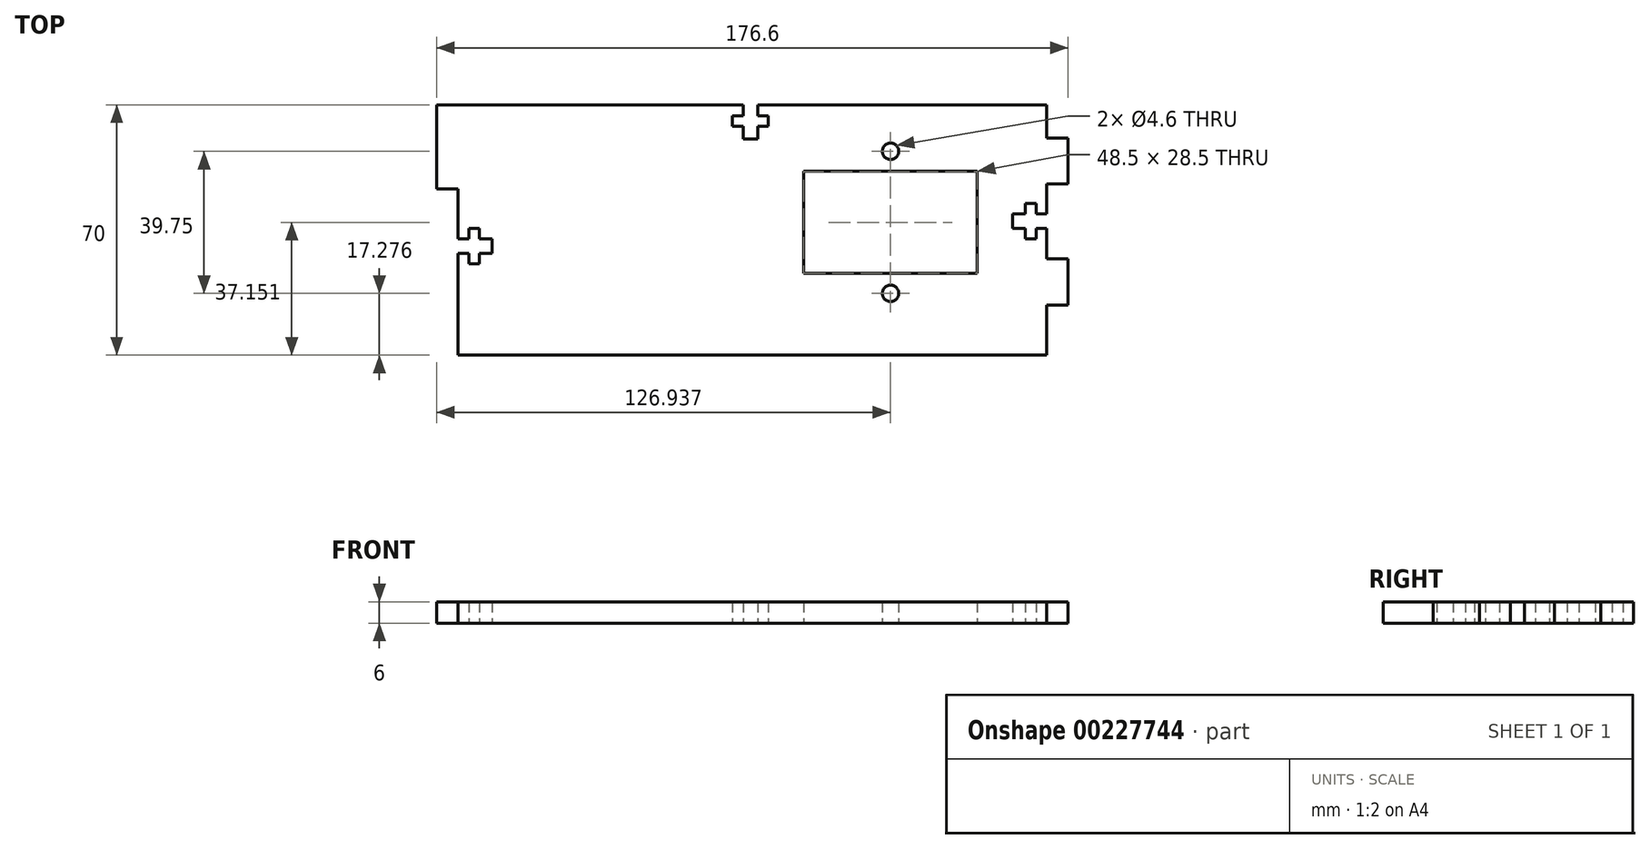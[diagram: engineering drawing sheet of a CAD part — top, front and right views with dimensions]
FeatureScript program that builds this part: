
annotation { "Feature Type Name" : "Feature", "Feature Type Description" : "" }
export const myFeature = defineFeature(function(context is Context, id is Id, definition is map)
    precondition{}
    {
        {
            var Q0;
            Q0=qCreatedBy(makeId("Top.planeOp"),FACE);
            var sketch = newSketch(context, id + "F0", { "sketchPlane" : qUnion([Q0])});
            skLineSegment(sketch, "E0.bottom", {"start": v(-82.3, 35) * mm, "end": v(82.3, 35) * mm});
            skLineSegment(sketch, "E0.top", {"start": v(-82.3, -35) * mm, "end": v(82.3, -35) * mm});
            skLineSegment(sketch, "E0.left", {"start": v(-82.3, 35) * mm, "end": v(-82.3, -35) * mm});
            skLineSegment(sketch, "E0.right", {"start": v(82.3, 35) * mm, "end": v(82.3, -35) * mm});
            skPoint(sketch, "E0.middle", {"position": v(0, 0) * mm});
            skLineSegment(sketch, "E1.bottom", {"start": v(82.3, 25.75) * mm, "end": v(88.3, 25.75) * mm});
            skLineSegment(sketch, "E1.top", {"start": v(82.3, 12.85) * mm, "end": v(88.3, 12.85) * mm});
            skLineSegment(sketch, "E1.left", {"start": v(82.3, 25.75) * mm, "end": v(82.3, 12.85) * mm});
            skLineSegment(sketch, "E1.right", {"start": v(88.3, 25.75) * mm, "end": v(88.3, 12.85) * mm});
            skLineSegment(sketch, "E2.bottom", {"start": v(82.3, -8.1) * mm, "end": v(88.3, -8.1) * mm});
            skLineSegment(sketch, "E2.top", {"start": v(82.3, -21) * mm, "end": v(88.3, -21) * mm});
            skLineSegment(sketch, "E2.left", {"start": v(82.3, -8.1) * mm, "end": v(82.3, -21) * mm});
            skLineSegment(sketch, "E2.right", {"start": v(88.3, -8.1) * mm, "end": v(88.3, -21) * mm});
            skLineSegment(sketch, "E3.bottom", {"start": v(-62.5, 35) * mm, "end": v(-23.3, 35) * mm});
            skLineSegment(sketch, "E3.top", {"start": v(-62.5, 41) * mm, "end": v(-23.3, 41) * mm});
            skLineSegment(sketch, "E3.left", {"start": v(-62.5, 35) * mm, "end": v(-62.5, 41) * mm});
            skLineSegment(sketch, "E3.right", {"start": v(-23.3, 35) * mm, "end": v(-23.3, 41) * mm});
            skLineSegment(sketch, "E4.bottom", {"start": v(22.1, 35) * mm, "end": v(61.3, 35) * mm});
            skLineSegment(sketch, "E4.top", {"start": v(22.1, 41) * mm, "end": v(61.3, 41) * mm});
            skLineSegment(sketch, "E4.left", {"start": v(22.1, 35) * mm, "end": v(22.1, 41) * mm});
            skLineSegment(sketch, "E4.right", {"start": v(61.3, 35) * mm, "end": v(61.3, 41) * mm});
            skLineSegment(sketch, "E5.bottom", {"start": v(-82.3, 35) * mm, "end": v(-88.3, 35) * mm});
            skLineSegment(sketch, "E5.top", {"start": v(-82.3, 11.5) * mm, "end": v(-88.3, 11.5) * mm});
            skLineSegment(sketch, "E5.left", {"start": v(-82.3, 35) * mm, "end": v(-82.3, 11.5) * mm});
            skLineSegment(sketch, "E5.right", {"start": v(-88.3, 35) * mm, "end": v(-88.3, 11.5) * mm});
            skLineSegment(sketch, "E6", {"start": v(-82.3, -2.5) * mm, "end": v(-79.3, -2.5) * mm});
            skLineSegment(sketch, "E7", {"start": v(-79.3, -2.5) * mm, "end": v(-79.3, 0.5) * mm});
            skLineSegment(sketch, "E8", {"start": v(-79.3, 0.5) * mm, "end": v(-76.3, 0.5) * mm});
            skLineSegment(sketch, "E9", {"start": v(-76.3, 0.5) * mm, "end": v(-76.3, -2.5) * mm});
            skLineSegment(sketch, "E10", {"start": v(-76.3, -2.5) * mm, "end": v(-72.8, -2.5) * mm});
            skLineSegment(sketch, "E11", {"start": v(-72.8, -2.5) * mm, "end": v(-72.8, -4.5) * mm});
            skLineSegment(sketch, "E12", {"start": v(-72.8, -4.5) * mm, "end": v(-82.3, -4.5) * mm, "construction": true});
            skLineSegment(sketch, "E13.MirrorCS", {"start": v(-82.3, -6.5) * mm, "end": v(-79.3, -6.5) * mm});
            skLineSegment(sketch, "E14.MirrorCS", {"start": v(-79.3, -6.5) * mm, "end": v(-79.3, -9.5) * mm});
            skLineSegment(sketch, "E15.MirrorCS", {"start": v(-76.3, -6.5) * mm, "end": v(-72.8, -6.5) * mm});
            skLineSegment(sketch, "E16.MirrorCS", {"start": v(-79.3, -9.5) * mm, "end": v(-76.3, -9.5) * mm});
            skLineSegment(sketch, "E17.MirrorCS", {"start": v(-72.8, -6.5) * mm, "end": v(-72.8, -4.5) * mm});
            skLineSegment(sketch, "E18.MirrorCS", {"start": v(-76.3, -9.5) * mm, "end": v(-76.3, -6.5) * mm});
            skLineSegment(sketch, "E19", {"start": v(72.8, 4.5) * mm, "end": v(76.3, 4.5) * mm});
            skLineSegment(sketch, "E20", {"start": v(76.3, 4.5) * mm, "end": v(76.3, 7.5) * mm});
            skLineSegment(sketch, "E21", {"start": v(76.3, 7.5) * mm, "end": v(79.3, 7.5) * mm});
            skLineSegment(sketch, "E22", {"start": v(79.3, 7.5) * mm, "end": v(79.3, 4.5) * mm});
            skLineSegment(sketch, "E23", {"start": v(79.3, 4.5) * mm, "end": v(82.3, 4.5) * mm});
            skLineSegment(sketch, "E24", {"start": v(82.3, 4.5) * mm, "end": v(82.3, 2.5) * mm});
            skLineSegment(sketch, "E25", {"start": v(82.3, 2.5) * mm, "end": v(72.8, 2.5) * mm, "construction": true});
            skLineSegment(sketch, "E26.MirrorCS", {"start": v(72.8, 0.5) * mm, "end": v(76.3, 0.5) * mm});
            skLineSegment(sketch, "E27.MirrorCS", {"start": v(76.3, 0.5) * mm, "end": v(76.3, -2.5) * mm});
            skLineSegment(sketch, "E28.MirrorCS", {"start": v(79.3, 0.5) * mm, "end": v(82.3, 0.5) * mm});
            skLineSegment(sketch, "E29.MirrorCS", {"start": v(76.3, -2.5) * mm, "end": v(79.3, -2.5) * mm});
            skLineSegment(sketch, "E30.MirrorCS", {"start": v(82.3, 0.5) * mm, "end": v(82.3, 2.5) * mm});
            skLineSegment(sketch, "E31.MirrorCS", {"start": v(79.3, -2.5) * mm, "end": v(79.3, 0.5) * mm});
            skLineSegment(sketch, "E32", {"start": v(72.8, 0.5) * mm, "end": v(72.8, 4.5) * mm});
            skLineSegment(sketch, "E33", {"start": v(-5.55, 32) * mm, "end": v(-2.55, 32) * mm});
            skLineSegment(sketch, "E34", {"start": v(-2.55, 32) * mm, "end": v(-2.55, 35) * mm});
            skLineSegment(sketch, "E35", {"start": v(-2.55, 35) * mm, "end": v(1.45, 35) * mm});
            skLineSegment(sketch, "E36", {"start": v(1.45, 35) * mm, "end": v(1.45, 32) * mm});
            skLineSegment(sketch, "E37", {"start": v(1.45, 32) * mm, "end": v(4.45, 32) * mm});
            skLineSegment(sketch, "E38.MirrorCS", {"start": v(-5.55, 29) * mm, "end": v(-2.55, 29) * mm});
            skLineSegment(sketch, "E39.MirrorCS", {"start": v(-2.55, 29) * mm, "end": v(-2.55, 25.5) * mm});
            skLineSegment(sketch, "E40.MirrorCS", {"start": v(1.45, 29) * mm, "end": v(4.45, 29) * mm});
            skLineSegment(sketch, "E41.MirrorCS", {"start": v(-2.55, 25.5) * mm, "end": v(1.45, 25.5) * mm});
            skLineSegment(sketch, "E42.MirrorCS", {"start": v(1.45, 25.5) * mm, "end": v(1.45, 29) * mm});
            skLineSegment(sketch, "E43", {"start": v(-5.55, 29) * mm, "end": v(-5.55, 32) * mm});
            skLineSegment(sketch, "E44", {"start": v(4.45, 29) * mm, "end": v(4.45, 32) * mm});
            skLineSegment(sketch, "E45.bottom", {"start": v(14.39, -12.1) * mm, "end": v(62.89, -12.1) * mm});
            skLineSegment(sketch, "E45.top", {"start": v(14.39, 16.4) * mm, "end": v(62.89, 16.4) * mm});
            skLineSegment(sketch, "E45.left", {"start": v(14.39, -12.1) * mm, "end": v(14.39, 16.4) * mm});
            skLineSegment(sketch, "E45.right", {"start": v(62.89, -12.1) * mm, "end": v(62.89, 16.4) * mm});
            skCircle(sketch, "E46", {"center": v(38.64, 22.03) * mm, "radius": 2.3 * mm});
            skPoint(sketch, "E46.centerSnap0", {"position": v(38.64, 16.4) * mm});
            skCircle(sketch, "E47", {"center": v(38.64, -17.72) * mm, "radius": 2.3 * mm});
            skPoint(sketch, "E47.centerSnap0", {"position": v(38.64, -12.1) * mm});
            skLineSegment(sketch, "E48", {"start": v(38.64, 22.03) * mm, "end": v(38.64, -17.72) * mm, "construction": true});
            skPoint(sketch, "E49", {"position": v(38.64, 2.15) * mm});
            skPoint(sketch, "E50", {"position": v(14.39, 2.15) * mm});
            skSolve(sketch);
        }
        {
            var Q0;
            {var subQ14=sQuery(id+"F0.wireOp",EDGE,"E0.top");Q0=makeQuery(id+"F0.imprint","IMPRINT",FACE,{"disambiguationData":[TD([[makeQuery(id+"F0.imprint","IMPRINT",EDGE,{"derivedFrom":subQ14}),1.0]])]});}
            var Q1;
            {var subQ0=sQuery(id+"F0.wireOp",EDGE,"E5.bottom");Q1=makeQuery(id+"F0.imprint","IMPRINT",FACE,{"disambiguationData":[TD([[makeQuery(id+"F0.imprint","IMPRINT",EDGE,{"derivedFrom":subQ0}),1.0]])]});}
            var Q2;
            Q2=makeQuery(id+"F0.imprint","IMPRINT",FACE,{"disambiguationData":[TD([[makeQuery(id+"F0.imprint","IMPRINT",EDGE,{"derivedFrom":sQuery(id+"F0.wireOp",EDGE,"E3.bottom")}),1.0]])]});
            var Q3;
            Q3=makeQuery(id+"F0.imprint","IMPRINT",FACE,{"disambiguationData":[TD([[makeQuery(id+"F0.imprint","IMPRINT",EDGE,{"derivedFrom":sQuery(id+"F0.wireOp",EDGE,"E4.bottom")}),1.0]])]});
            var Q4;
            Q4=makeQuery(id+"F0.imprint","IMPRINT",FACE,{"disambiguationData":[TD([[makeQuery(id+"F0.imprint","IMPRINT",EDGE,{"derivedFrom":sQuery(id+"F0.wireOp",EDGE,"E1.bottom")}),-1.0]])]});
            var Q5;
            Q5=makeQuery(id+"F0.imprint","IMPRINT",FACE,{"disambiguationData":[TD([[makeQuery(id+"F0.imprint","IMPRINT",EDGE,{"derivedFrom":sQuery(id+"F0.wireOp",EDGE,"E2.bottom")}),-1.0]])]});
            extrude(context, id + "F1", {"entities" : qUnion([Q0, Q1, Q2, Q3, Q4, Q5]), "depth" : 6 * mm});
        }
    });
